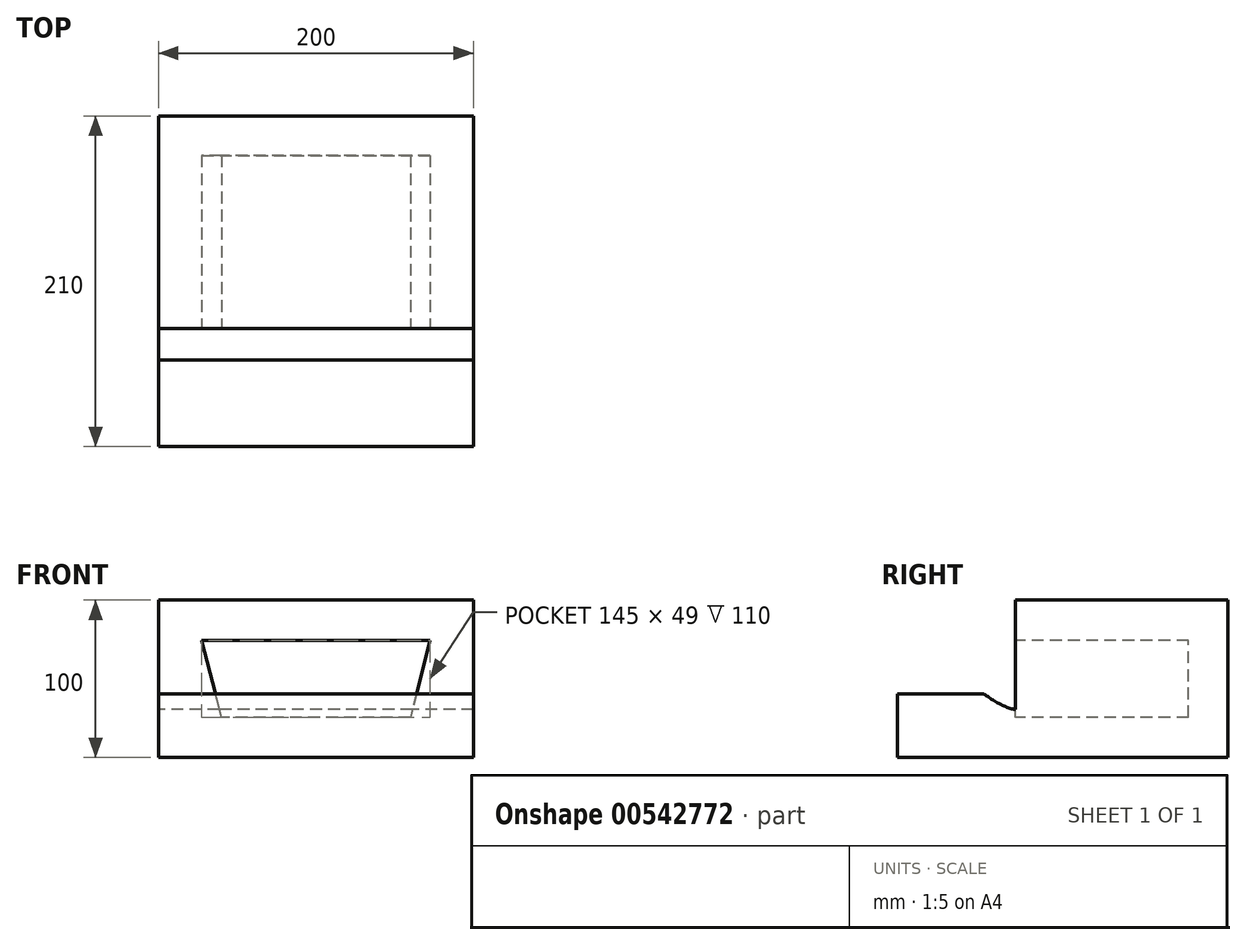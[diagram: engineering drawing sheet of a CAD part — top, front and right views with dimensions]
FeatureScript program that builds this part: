
annotation { "Feature Type Name" : "Feature", "Feature Type Description" : "" }
export const myFeature = defineFeature(function(context is Context, id is Id, definition is map)
    precondition{}
    {
        {
            var Q0;
            Q0=qCreatedBy(makeId("Front.planeOp"),FACE);
            var sketch = newSketch(context, id + "F0", { "sketchPlane" : qUnion([Q0])});
            skLineSegment(sketch, "E0.bottom", {"start": v(-100, 50) * mm, "end": v(100, 50) * mm});
            skLineSegment(sketch, "E0.top", {"start": v(-100, -50) * mm, "end": v(100, -50) * mm});
            skLineSegment(sketch, "E0.left", {"start": v(-100, 50) * mm, "end": v(-100, -50) * mm});
            skLineSegment(sketch, "E0.right", {"start": v(100, 50) * mm, "end": v(100, -50) * mm});
            skPoint(sketch, "E0.middle", {"position": v(0, 0) * mm});
            skLineSegment(sketch, "E1", {"start": v(-72.5, 24.5) * mm, "end": v(72.5, 24.5) * mm});
            skLineSegment(sketch, "E2", {"start": v(72.5, 24.5) * mm, "end": v(60, -24.5) * mm});
            skLineSegment(sketch, "E3", {"start": v(60, -24.5) * mm, "end": v(-60, -24.5) * mm});
            skLineSegment(sketch, "E4", {"start": v(-60, -24.5) * mm, "end": v(-72.5, 24.5) * mm});
            skPoint(sketch, "E5", {"position": v(0, 24.5) * mm});
            skPoint(sketch, "E6", {"position": v(0, -24.5) * mm});
            skPoint(sketch, "E7", {"position": v(66.25, 0) * mm});
            skSolve(sketch);
        }
        {
            var Q0;
            Q0=makeQuery(id+"F0.imprint","IMPRINT",FACE,{"disambiguationData":[TD([[makeQuery(id+"F0.imprint","IMPRINT",EDGE,{"derivedFrom":sQuery(id+"F0.wireOp",EDGE,"E0.bottom")}),-1.0]])]});
            extrude(context, id + "F1", {"entities" : qUnion([Q0]), "oppositeDirection" : true, "depth" : 110 * mm, "offsetDistance" : 25 * mm});
        }
        {
            var Q0;
            Q0=makeQuery(id+"F1.opExtrude","CAP_FACE",FACE,{"disambiguationData":[OSD([sQuery(id+"F0.wireOp",EDGE,"E0.bottom"),sQuery(id+"F0.wireOp",EDGE,"E0.top"),sQuery(id+"F0.wireOp",EDGE,"E0.left"),sQuery(id+"F0.wireOp",EDGE,"E0.right"),sQuery(id+"F0.wireOp",EDGE,"E1"),sQuery(id+"F0.wireOp",EDGE,"E2"),sQuery(id+"F0.wireOp",EDGE,"E3"),sQuery(id+"F0.wireOp",EDGE,"E4")])],"isStart":false});
            var sketch = newSketch(context, id + "F2", { "sketchPlane" : qUnion([Q0])});
            skLineSegment(sketch, "E8", {"start": v(-100, 50) * mm, "end": v(100, 50) * mm});
            skLineSegment(sketch, "E9", {"start": v(100, 50) * mm, "end": v(100, -50) * mm});
            skLineSegment(sketch, "E10", {"start": v(100, -50) * mm, "end": v(-100, -50) * mm});
            skLineSegment(sketch, "E11", {"start": v(-100, -50) * mm, "end": v(-100, 50) * mm});
            skSolve(sketch);
        }
        {
            var Q0;
            Q0 = qSketchRegion(id + "F2", true);
            extrude(context, id + "F3", {"entities" : qUnion([Q0]), "operationType" : NewBodyOperationType.ADD, "depth" : 25 * mm, "offsetDistance" : 25 * mm});
        }
        {
            var Q0;
            Q0=qCreatedBy(makeId("Right.planeOp"),FACE);
            var sketch = newSketch(context, id + "F4", { "sketchPlane" : qUnion([Q0])});
            skLineSegment(sketch, "E12", {"start": v(0, -50) * mm, "end": v(0, -19.5) * mm});
            skFitSpline(sketch, "E13", {"points": [v(0, -19.5) * mm, v(-20, -9.5) * mm], "startDerivative": vector(-17.51, 1.23) * mm, "endDerivative": vector(-11.36, 8.9) * mm});
            skLineSegment(sketch, "E14", {"start": v(-20, -9.5) * mm, "end": v(-75, -9.5) * mm});
            skLineSegment(sketch, "E15", {"start": v(-75, -9.5) * mm, "end": v(-75, -50) * mm});
            skLineSegment(sketch, "E16", {"start": v(-75, -50) * mm, "end": v(0, -50) * mm});
            skSolve(sketch);
        }
        {
            var Q0;
            Q0 = qSketchRegion(id + "F4", true);
            extrude(context, id + "F5", {"entities" : qUnion([Q0]), "operationType" : NewBodyOperationType.ADD, "endBound" : BoundingType.SYMMETRIC, "depth" : 200 * mm, "offsetDistance" : 25 * mm});
        }
    });
